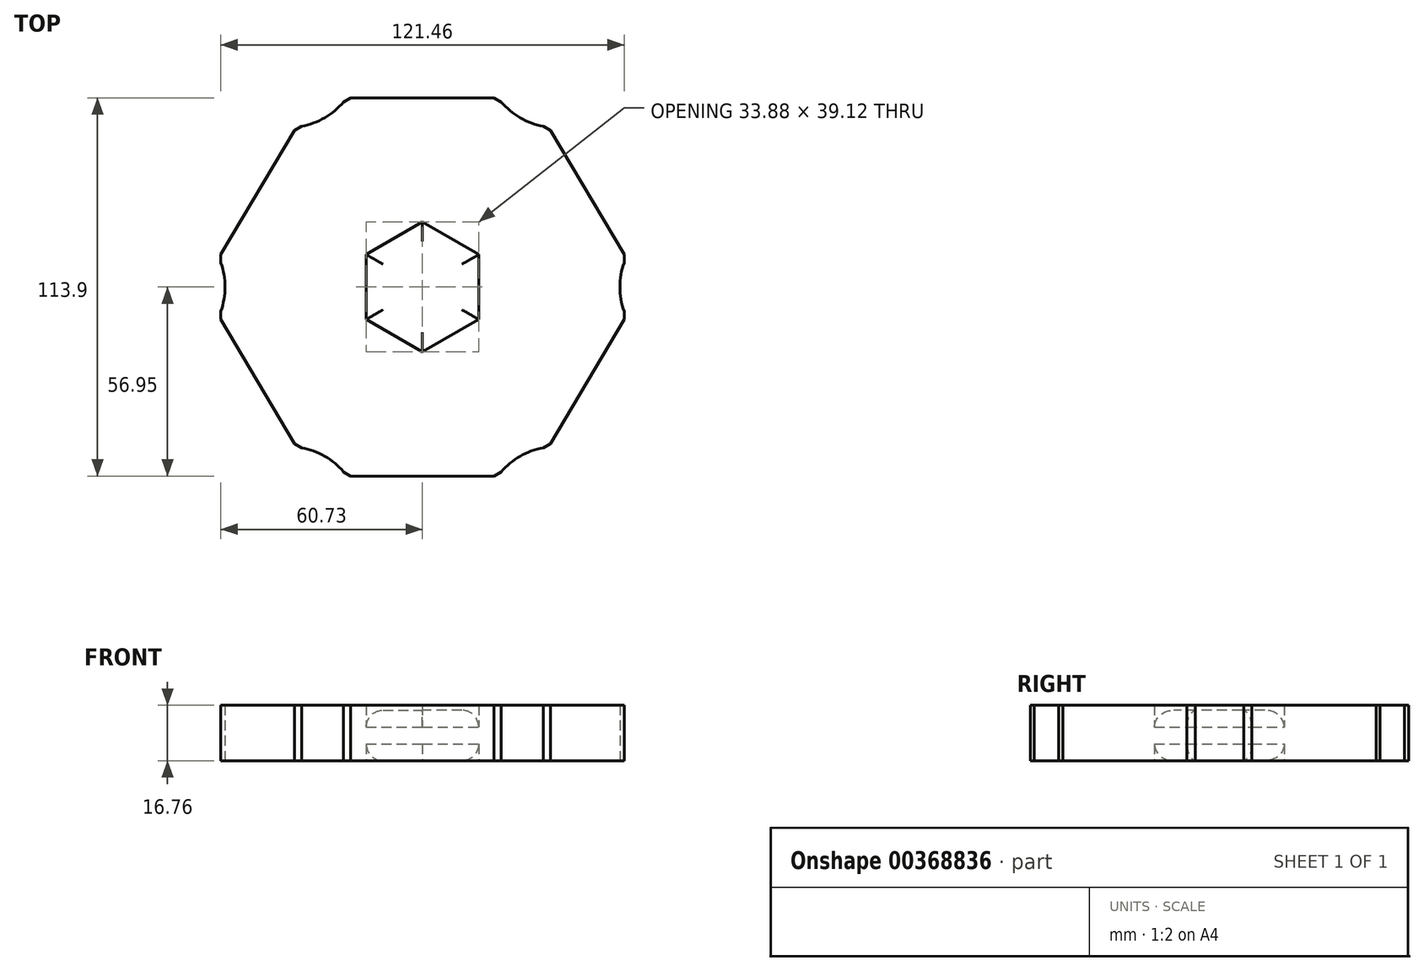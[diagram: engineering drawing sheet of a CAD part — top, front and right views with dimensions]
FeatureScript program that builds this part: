
annotation { "Feature Type Name" : "Feature", "Feature Type Description" : "" }
export const myFeature = defineFeature(function(context is Context, id is Id, definition is map)
    precondition{}
    {
        {
            var Q0;
            Q0=qCreatedBy(makeId("Top.planeOp"),FACE);
            var sketch = newSketch(context, id + "F0", { "sketchPlane" : qUnion([Q0])});
            skCircle(sketch, "E0.cCircle", {"center": v(0, 0) * mm, "radius": 16.94 * mm, "construction": true});
            skLineSegment(sketch, "E0.0", {"start": v(16.94, -9.78) * mm, "end": v(0, -19.56) * mm});
            skLineSegment(sketch, "E0.1", {"start": v(0, -19.56) * mm, "end": v(-16.94, -9.78) * mm});
            skLineSegment(sketch, "E0.2", {"start": v(-16.94, -9.78) * mm, "end": v(-16.94, 9.78) * mm});
            skLineSegment(sketch, "E0.3", {"start": v(-16.94, 9.78) * mm, "end": v(0, 19.56) * mm});
            skLineSegment(sketch, "E0.4", {"start": v(0, 19.56) * mm, "end": v(16.94, 9.78) * mm});
            skLineSegment(sketch, "E0.5", {"start": v(16.94, 9.78) * mm, "end": v(16.94, -9.78) * mm});
            skPoint(sketch, "E0.0.midPoint", {"position": v(8.47, -14.67) * mm});
            skLineSegment(sketch, "E1.bottom", {"start": v(60.73, 9.78) * mm, "end": v(17.56, 9.78) * mm});
            skLineSegment(sketch, "E1.top", {"start": v(60.73, -9.78) * mm, "end": v(17.56, -9.78) * mm});
            skLineSegment(sketch, "E1.left", {"start": v(60.73, 9.78) * mm, "end": v(60.73, -9.78) * mm});
            skLineSegment(sketch, "E1.right", {"start": v(17.56, 9.78) * mm, "end": v(17.56, -9.78) * mm});
            skPoint(sketch, "E1.middle", {"position": v(39.14, 0) * mm});
            skLineSegment(sketch, "E2.MirrorCS", {"start": v(60.73, -9.78) * mm, "end": v(60.73, 9.78) * mm});
            skLineSegment(sketch, "E3.MirrorCS", {"start": v(-60.73, 9.78) * mm, "end": v(-17.56, 9.78) * mm});
            skLineSegment(sketch, "E4.MirrorCS", {"start": v(-60.73, -9.78) * mm, "end": v(-17.56, -9.78) * mm});
            skLineSegment(sketch, "E5.MirrorCS", {"start": v(-60.73, 9.78) * mm, "end": v(-60.73, -9.78) * mm});
            skLineSegment(sketch, "E6", {"start": v(-16.94, -9.78) * mm, "end": v(-38.53, -47.17) * mm});
            skLineSegment(sketch, "E7", {"start": v(0, -19.56) * mm, "end": v(-21.59, -56.95) * mm});
            skLineSegment(sketch, "E8", {"start": v(-38.53, -47.17) * mm, "end": v(-21.59, -56.95) * mm});
            skLineSegment(sketch, "E9.MirrorCS", {"start": v(0, -19.56) * mm, "end": v(21.59, -56.95) * mm});
            skLineSegment(sketch, "E10.MirrorCS", {"start": v(16.94, -9.78) * mm, "end": v(38.53, -47.17) * mm});
            skLineSegment(sketch, "E11.MirrorCS", {"start": v(38.53, -47.17) * mm, "end": v(21.59, -56.95) * mm});
            skLineSegment(sketch, "E12", {"start": v(0, 19.56) * mm, "end": v(-21.6, 56.95) * mm});
            skLineSegment(sketch, "E13", {"start": v(-16.94, 9.78) * mm, "end": v(-38.53, 47.17) * mm});
            skLineSegment(sketch, "E14", {"start": v(-38.53, 47.17) * mm, "end": v(-21.6, 56.95) * mm});
            skLineSegment(sketch, "E15.MirrorCS", {"start": v(0, 19.56) * mm, "end": v(21.6, 56.95) * mm});
            skLineSegment(sketch, "E16.MirrorCS", {"start": v(16.94, 9.78) * mm, "end": v(38.53, 47.17) * mm});
            skLineSegment(sketch, "E17.MirrorCS", {"start": v(38.53, 47.17) * mm, "end": v(21.6, 56.95) * mm});
            skLineSegment(sketch, "E18", {"start": v(-21.6, 56.95) * mm, "end": v(21.6, 56.95) * mm});
            skLineSegment(sketch, "E19", {"start": v(38.53, 47.17) * mm, "end": v(60.73, 9.78) * mm});
            skLineSegment(sketch, "E20", {"start": v(60.73, -9.78) * mm, "end": v(38.53, -47.17) * mm});
            skLineSegment(sketch, "E21", {"start": v(21.59, -56.95) * mm, "end": v(-21.59, -56.95) * mm});
            skLineSegment(sketch, "E22", {"start": v(-38.53, -47.17) * mm, "end": v(-60.73, -9.78) * mm});
            skLineSegment(sketch, "E23", {"start": v(-60.73, 9.78) * mm, "end": v(-38.53, 47.17) * mm});
            skPoint(sketch, "E24.start.orphan", {"position": v(-30.06, 52.06) * mm});
            skCircle(sketch, "E25", {"center": v(-40.22, 69.66) * mm, "radius": 21.59 * mm});
            skCircle(sketch, "E26.MirrorC", {"center": v(40.22, 69.66) * mm, "radius": 21.59 * mm});
            skPoint(sketch, "E27.endSnap0", {"position": v(60.73, 0) * mm});
            skPoint(sketch, "E27.end.orphan", {"position": v(76.8, 0) * mm});
            skPoint(sketch, "E27.start.orphan", {"position": v(60.73, 0) * mm});
            skLineSegment(sketch, "E28", {"start": v(76.8, 0) * mm, "end": v(81.05, 0) * mm});
            skCircle(sketch, "E29", {"center": v(81.05, 0) * mm, "radius": 21.59 * mm});
            skPoint(sketch, "E30.endSnap0", {"position": v(-60.73, 0) * mm});
            skCircle(sketch, "E31", {"center": v(-81.05, 0) * mm, "radius": 21.59 * mm});
            skCircle(sketch, "E32", {"center": v(40.22, -69.66) * mm, "radius": 21.59 * mm});
            skCircle(sketch, "E33.MirrorC", {"center": v(-40.22, -69.66) * mm, "radius": 21.59 * mm});
            skPoint(sketch, "E30.start.orphan", {"position": v(-60.73, 0) * mm});
            skPoint(sketch, "E34.MirrorCS.start.orphan", {"position": v(-30.06, -52.06) * mm});
            skPoint(sketch, "E35.start.orphan", {"position": v(30.06, -52.06) * mm});
            skPoint(sketch, "E36.MirrorCS.start.orphan", {"position": v(30.06, 52.06) * mm});
            skCircle(sketch, "E37", {"center": v(-40.22, 69.66) * mm, "radius": 17.78 * mm});
            skCircle(sketch, "E38.MirrorC", {"center": v(40.22, 69.66) * mm, "radius": 17.78 * mm});
            skCircle(sketch, "E39", {"center": v(-81.05, 0) * mm, "radius": 17.78 * mm});
            skCircle(sketch, "E40", {"center": v(81.05, 0) * mm, "radius": 17.78 * mm});
            skCircle(sketch, "E41", {"center": v(-40.22, -69.66) * mm, "radius": 19.05 * mm});
            skCircle(sketch, "E42.MirrorC", {"center": v(40.22, -69.66) * mm, "radius": 19.05 * mm});
            skSolve(sketch);
        }
        {
            var Q0;
            Q0=makeQuery(id+"F0.imprint","IMPRINT",FACE,{"disambiguationData":[TD([[makeQuery(id+"F0.imprint","IMPRINT",EDGE,{"derivedFrom":sQuery(id+"F0.wireOp",EDGE,"E0.0")}),-1.0]])]});
            extrude(context, id + "F1", {"entities" : qUnion([Q0]), "depth" : 15.24 * mm});
        }
        {
            var Q0;
            Q0=makeQuery(id+"F1.opExtrude","CAP_FACE",FACE,{"disambiguationData":[OSD([sQuery(id+"F0.wireOp",EDGE,"E0.0"),sQuery(id+"F0.wireOp",EDGE,"E0.1"),sQuery(id+"F0.wireOp",EDGE,"E0.2"),sQuery(id+"F0.wireOp",EDGE,"E0.3"),sQuery(id+"F0.wireOp",EDGE,"E0.4"),sQuery(id+"F0.wireOp",EDGE,"E0.5")])],"isStart":false});
            fillet(context, id + "F2", {"entities" : qUnion([Q0]), "radius" : 5.08 * mm, "tangentPropagation" : true, "allowEdgeOverflow" : false});
        }
        {
            var Q0;
            Q0=makeQuery(id+"F1.opExtrude","CAP_FACE",FACE,{"disambiguationData":[OSD([sQuery(id+"F0.wireOp",EDGE,"E0.0"),sQuery(id+"F0.wireOp",EDGE,"E0.1"),sQuery(id+"F0.wireOp",EDGE,"E0.2"),sQuery(id+"F0.wireOp",EDGE,"E0.3"),sQuery(id+"F0.wireOp",EDGE,"E0.4"),sQuery(id+"F0.wireOp",EDGE,"E0.5")])],"isStart":true});
            fillet(context, id + "F3", {"entities" : qUnion([Q0]), "radius" : 5.08 * mm, "tangentPropagation" : true, "allowEdgeOverflow" : false});
        }
        {
            var Q0;
            Q0=makeQuery(id+"F0.imprint","IMPRINT",FACE,{"disambiguationData":[TD([[makeQuery(id+"F0.imprint","IMPRINT",EDGE,{"derivedFrom":sQuery(id+"F0.wireOp",EDGE,"E0.2")}),1.0]])]});
            var Q1;
            Q1=makeQuery(id+"F0.imprint","IMPRINT",FACE,{"disambiguationData":[TD([[makeQuery(id+"F0.imprint","IMPRINT",EDGE,{"derivedFrom":sQuery(id+"F0.wireOp",EDGE,"E0.3")}),1.0]])]});
            var Q2;
            Q2=makeQuery(id+"F0.imprint","IMPRINT",FACE,{"disambiguationData":[TD([[makeQuery(id+"F0.imprint","IMPRINT",EDGE,{"derivedFrom":sQuery(id+"F0.wireOp",EDGE,"E12")}),-1.0]])]});
            var Q3;
            Q3=makeQuery(id+"F0.imprint","IMPRINT",FACE,{"disambiguationData":[TD([[makeQuery(id+"F0.imprint","IMPRINT",EDGE,{"derivedFrom":sQuery(id+"F0.wireOp",EDGE,"E0.5")}),1.0]])]});
            var Q4;
            Q4=makeQuery(id+"F0.imprint","IMPRINT",FACE,{"disambiguationData":[TD([[makeQuery(id+"F0.imprint","IMPRINT",EDGE,{"derivedFrom":sQuery(id+"F0.wireOp",EDGE,"E0.4")}),1.0]])]});
            var Q5;
            Q5=makeQuery(id+"F0.imprint","IMPRINT",FACE,{"disambiguationData":[TD([[makeQuery(id+"F0.imprint","IMPRINT",EDGE,{"derivedFrom":sQuery(id+"F0.wireOp",EDGE,"E1.right")}),1.0]])]});
            var Q6;
            Q6=makeQuery(id+"F0.imprint","IMPRINT",FACE,{"disambiguationData":[TD([[makeQuery(id+"F0.imprint","IMPRINT",EDGE,{"derivedFrom":sQuery(id+"F0.wireOp",EDGE,"E0.0")}),1.0]])]});
            var Q7;
            Q7=makeQuery(id+"F0.imprint","IMPRINT",FACE,{"disambiguationData":[TD([[makeQuery(id+"F0.imprint","IMPRINT",EDGE,{"derivedFrom":sQuery(id+"F0.wireOp",EDGE,"E7")}),1.0]])]});
            var Q8;
            Q8=makeQuery(id+"F0.imprint","IMPRINT",FACE,{"disambiguationData":[TD([[makeQuery(id+"F0.imprint","IMPRINT",EDGE,{"derivedFrom":sQuery(id+"F0.wireOp",EDGE,"E0.1")}),1.0]])]});
            extrude(context, id + "F4", {"entities" : qUnion([Q0, Q1, Q2, Q3, Q4, Q5, Q6, Q7, Q8]), "operationType" : NewBodyOperationType.ADD, "depth" : 16.76 * mm});
        }
    });
